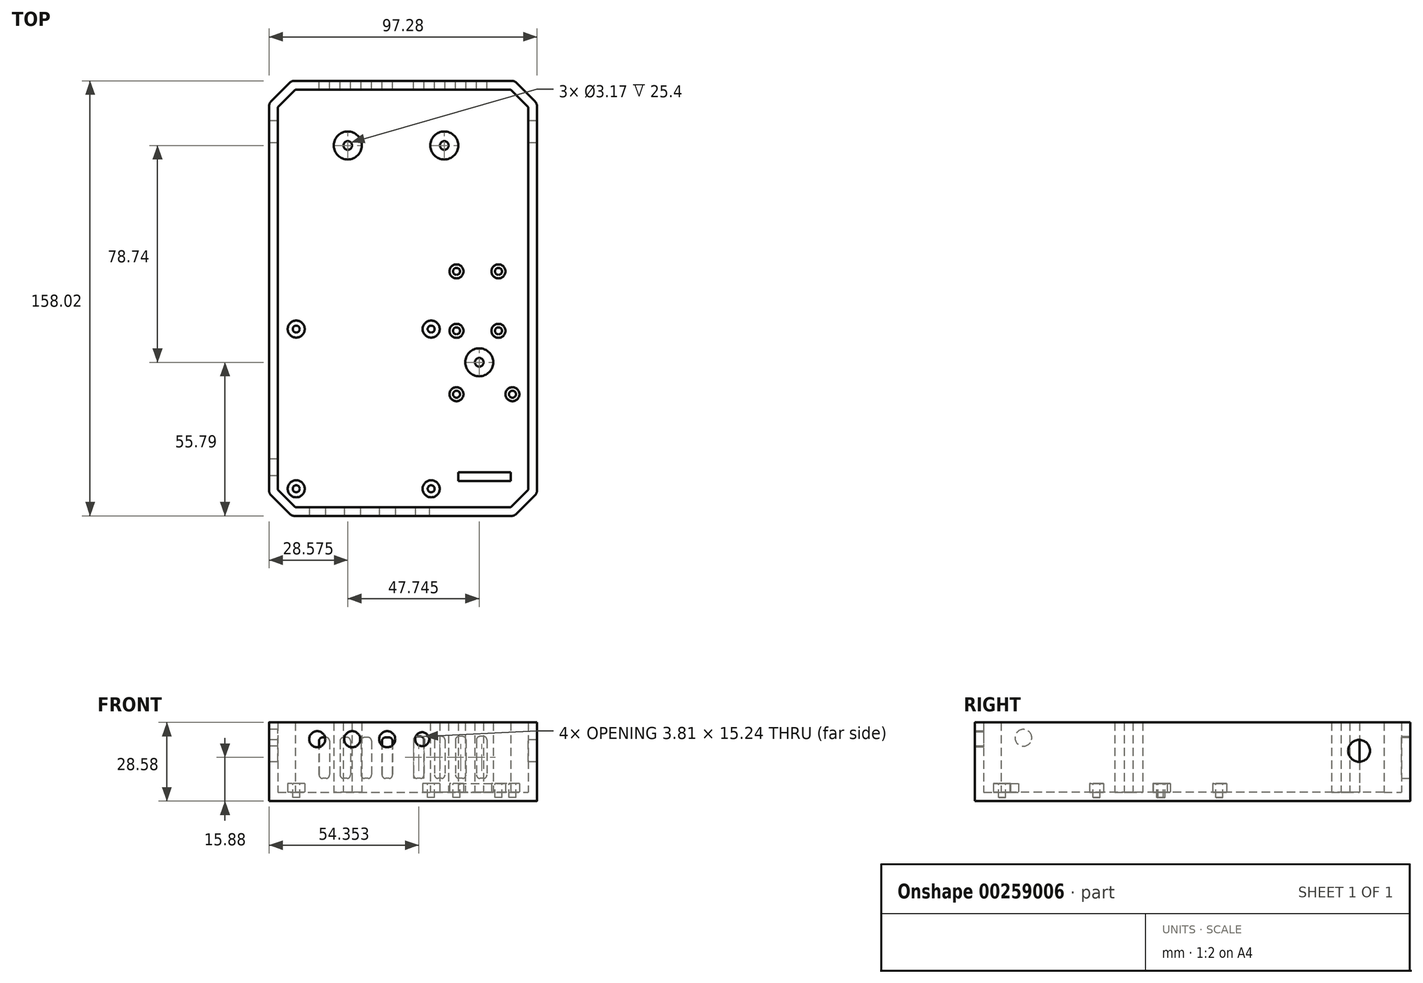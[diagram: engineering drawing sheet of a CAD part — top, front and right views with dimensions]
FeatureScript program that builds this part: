
annotation { "Feature Type Name" : "Feature", "Feature Type Description" : "" }
export const myFeature = defineFeature(function(context is Context, id is Id, definition is map)
    precondition{}
    {
        {
            var Q0;
            Q0=qCreatedBy(makeId("Top.planeOp"),FACE);
            var sketch = newSketch(context, id + "F0", { "sketchPlane" : qUnion([Q0])});
            skLineSegment(sketch, "E0.bottom", {"start": v(-25, 46.5) * mm, "end": v(25, 46.5) * mm});
            skLineSegment(sketch, "E0.top", {"start": v(-25, -38.5) * mm, "end": v(25, -38.5) * mm});
            skLineSegment(sketch, "E0.left", {"start": v(-28, 43.5) * mm, "end": v(-28, -35.5) * mm});
            skLineSegment(sketch, "E0.right", {"start": v(28, 43.5) * mm, "end": v(28, -35.5) * mm});
            skCircle(sketch, "E1", {"center": v(-24.5, -35) * mm, "radius": 3.1 * mm});
            skCircle(sketch, "E2", {"center": v(24.5, -35) * mm, "radius": 3.1 * mm});
            skCircle(sketch, "E3", {"center": v(24.5, 23) * mm, "radius": 3.1 * mm});
            skCircle(sketch, "E4", {"center": v(-24.5, 23) * mm, "radius": 3.1 * mm});
            skCircle(sketch, "E5", {"center": v(-24.5, 23) * mm, "radius": 1.38 * mm});
            skCircle(sketch, "E6", {"center": v(24.5, 23) * mm, "radius": 1.38 * mm});
            skCircle(sketch, "E7", {"center": v(24.5, -35) * mm, "radius": 1.38 * mm});
            skCircle(sketch, "E8", {"center": v(-24.5, -35) * mm, "radius": 1.38 * mm});
            skPoint(sketch, "E9.visualSharp", {"position": v(-28, 46.5) * mm});
            skArc(sketch, "E9.filletArc", {"start": v(-25, 46.5) * mm, "mid": v(-27.12, 45.62) * mm, "end": v(-28, 43.5) * mm});
            skPoint(sketch, "E10.visualSharp", {"position": v(28, 46.5) * mm});
            skArc(sketch, "E10.filletArc", {"start": v(28, 43.5) * mm, "mid": v(27.12, 45.62) * mm, "end": v(25, 46.5) * mm});
            skPoint(sketch, "E11.visualSharp", {"position": v(-28, -38.5) * mm});
            skArc(sketch, "E11.filletArc", {"start": v(-28, -35.5) * mm, "mid": v(-27.12, -37.62) * mm, "end": v(-25, -38.5) * mm});
            skPoint(sketch, "E12.visualSharp", {"position": v(28, -38.5) * mm});
            skArc(sketch, "E12.filletArc", {"start": v(25, -38.5) * mm, "mid": v(27.12, -37.62) * mm, "end": v(28, -35.5) * mm});
            skSolve(sketch);
        }
        {
            var Q0;
            Q0=qCreatedBy(makeId("Top.planeOp"),FACE);
            var sketch = newSketch(context, id + "F1", { "sketchPlane" : qUnion([Q0])});
            skLineSegment(sketch, "E13.bottom", {"start": v(31.17, 46.5) * mm, "end": v(51.5, 46.5) * mm});
            skLineSegment(sketch, "E13.top", {"start": v(31.18, 19.83) * mm, "end": v(51.5, 19.83) * mm});
            skLineSegment(sketch, "E13.left", {"start": v(31.17, 46.5) * mm, "end": v(31.18, 19.83) * mm});
            skLineSegment(sketch, "E13.right", {"start": v(51.5, 46.5) * mm, "end": v(51.5, 19.83) * mm});
            skCircle(sketch, "E14", {"center": v(33.72, 43.96) * mm, "radius": 1.14 * mm});
            skCircle(sketch, "E15", {"center": v(48.95, 43.96) * mm, "radius": 1.14 * mm});
            skCircle(sketch, "E16", {"center": v(48.95, 22.37) * mm, "radius": 1.14 * mm});
            skCircle(sketch, "E17", {"center": v(33.72, 22.37) * mm, "radius": 1.14 * mm});
            skSolve(sketch);
        }
        {
            var Q0;
            Q0=qCreatedBy(makeId("Top.planeOp"),FACE);
            var sketch = newSketch(context, id + "F2", { "sketchPlane" : qUnion([Q0])});
            skLineSegment(sketch, "E18.bottom", {"start": v(31.18, 1.89) * mm, "end": v(56.58, 1.89) * mm});
            skLineSegment(sketch, "E18.top", {"start": v(31.18, -32.15) * mm, "end": v(56.58, -32.15) * mm});
            skLineSegment(sketch, "E18.left", {"start": v(31.18, 1.89) * mm, "end": v(31.18, -32.15) * mm});
            skLineSegment(sketch, "E18.right", {"start": v(56.57, 1.89) * mm, "end": v(56.57, -32.15) * mm});
            skCircle(sketch, "E19", {"center": v(33.72, -0.65) * mm, "radius": 1.14 * mm});
            skCircle(sketch, "E20", {"center": v(54.04, -0.65) * mm, "radius": 1.14 * mm});
            skSolve(sketch);
        }
        {
            var Q0;
            Q0=qCreatedBy(makeId("Top.planeOp"),FACE);
            var sketch = newSketch(context, id + "F3", { "sketchPlane" : qUnion([Q0])});
            skLineSegment(sketch, "E21.bottom", {"start": v(-24.83, 110) * mm, "end": v(53.4, 110) * mm});
            skLineSegment(sketch, "E21.top", {"start": v(-24.82, -41.68) * mm, "end": v(53.4, -41.68) * mm});
            skLineSegment(sketch, "E21.left", {"start": v(-31.18, 103.65) * mm, "end": v(-31.17, -35.33) * mm});
            skLineSegment(sketch, "E21.right", {"start": v(59.75, 103.65) * mm, "end": v(59.75, -35.33) * mm});
            skLineSegment(sketch, "E22", {"start": v(-31.18, 103.65) * mm, "end": v(-24.83, 110) * mm});
            skLineSegment(sketch, "E23", {"start": v(53.4, 110) * mm, "end": v(59.75, 103.65) * mm});
            skLineSegment(sketch, "E24", {"start": v(-31.17, -35.33) * mm, "end": v(-24.82, -41.68) * mm});
            skLineSegment(sketch, "E25", {"start": v(53.4, -41.67) * mm, "end": v(59.75, -35.33) * mm});
            skPoint(sketch, "E26.orphan", {"position": v(-31.18, 110) * mm});
            skPoint(sketch, "E27.orphan", {"position": v(59.75, 110) * mm});
            skPoint(sketch, "E28.orphan", {"position": v(59.75, -41.68) * mm});
            skPoint(sketch, "E29.orphan", {"position": v(-31.17, -41.68) * mm});
            skLineSegment(sketch, "E30.0", {"start": v(-34.35, 104.97) * mm, "end": v(-26.14, 113.18) * mm});
            skLineSegment(sketch, "E30.1", {"start": v(-26.14, 113.18) * mm, "end": v(54.72, 113.18) * mm});
            skLineSegment(sketch, "E30.2", {"start": v(-34.35, 104.97) * mm, "end": v(-34.35, -36.64) * mm});
            skLineSegment(sketch, "E30.3", {"start": v(54.72, 113.18) * mm, "end": v(62.92, 104.97) * mm});
            skLineSegment(sketch, "E30.4", {"start": v(-34.35, -36.64) * mm, "end": v(-26.14, -44.85) * mm});
            skLineSegment(sketch, "E30.5", {"start": v(-26.14, -44.85) * mm, "end": v(54.72, -44.85) * mm});
            skLineSegment(sketch, "E30.6", {"start": v(54.72, -44.85) * mm, "end": v(62.92, -36.64) * mm});
            skLineSegment(sketch, "E30.7", {"start": v(62.92, 104.97) * mm, "end": v(62.92, -36.64) * mm});
            skSolve(sketch);
        }
        {
            var Q0;
            Q0=makeQuery(id+"F3.imprint","IMPRINT",FACE,{"disambiguationData":[TD([[makeQuery(id+"F3.imprint","IMPRINT",EDGE,{"derivedFrom":sQuery(id+"F3.wireOp",EDGE,"E21.bottom")}),-1.0]])]});
            var Q1;
            Q1=makeQuery(id+"F3.imprint","IMPRINT",FACE,{"disambiguationData":[TD([[makeQuery(id+"F3.imprint","IMPRINT",EDGE,{"derivedFrom":sQuery(id+"F3.wireOp",EDGE,"E21.bottom")}),1.0]])]});
            extrude(context, id + "F4", {"entities" : qUnion([Q0, Q1]), "oppositeDirection" : true, "depth" : 3.17 * mm});
        }
        {
            var Q0;
            Q0=makeQuery(id+"F3.imprint","IMPRINT",FACE,{"disambiguationData":[TD([[makeQuery(id+"F3.imprint","IMPRINT",EDGE,{"derivedFrom":sQuery(id+"F3.wireOp",EDGE,"E21.bottom")}),1.0]])]});
            extrude(context, id + "F5", {"entities" : qUnion([Q0]), "operationType" : NewBodyOperationType.ADD, "depth" : 25.4 * mm});
        }
        {
            var Q0;
            Q0=makeQuery(id+"F3.imprint","IMPRINT",FACE,{"disambiguationData":[TD([[makeQuery(id+"F3.imprint","IMPRINT",EDGE,{"derivedFrom":sQuery(id+"F3.wireOp",EDGE,"E21.bottom")}),-1.0]])]});
            var sketch = newSketch(context, id + "F6", { "sketchPlane" : qUnion([Q0])});
            skCircle(sketch, "E31", {"center": v(-24.5, 23) * mm, "radius": 3.1 * mm});
            skCircle(sketch, "E32", {"center": v(24.5, 23) * mm, "radius": 3.1 * mm});
            skCircle(sketch, "E33", {"center": v(-24.5, -35) * mm, "radius": 3.1 * mm});
            skCircle(sketch, "E34", {"center": v(24.5, -35) * mm, "radius": 3.1 * mm});
            skCircle(sketch, "E35", {"center": v(33.72, 43.96) * mm, "radius": 2.54 * mm});
            skCircle(sketch, "E36", {"center": v(48.95, 43.96) * mm, "radius": 2.54 * mm});
            skCircle(sketch, "E37", {"center": v(33.72, 22.37) * mm, "radius": 2.54 * mm});
            skCircle(sketch, "E38", {"center": v(48.95, 22.37) * mm, "radius": 2.54 * mm});
            skCircle(sketch, "E39", {"center": v(33.72, -0.65) * mm, "radius": 2.54 * mm});
            skCircle(sketch, "E40", {"center": v(54.04, -0.65) * mm, "radius": 2.54 * mm});
            skLineSegment(sketch, "E41.bottom", {"start": v(34.35, -32.15) * mm, "end": v(53.4, -32.15) * mm});
            skLineSegment(sketch, "E41.top", {"start": v(34.35, -28.97) * mm, "end": v(53.4, -28.97) * mm});
            skLineSegment(sketch, "E41.left", {"start": v(34.35, -32.15) * mm, "end": v(34.35, -28.97) * mm});
            skLineSegment(sketch, "E41.right", {"start": v(53.4, -32.15) * mm, "end": v(53.4, -28.97) * mm});
            skSolve(sketch);
        }
        {
            var Q0;
            Q0 = qSketchRegion(id + "F6", true);
            var Q1;
            Q1=makeQuery(id+"F0.imprint","IMPRINT",FACE,{"disambiguationData":[TD([[makeQuery(id+"F0.imprint","IMPRINT",EDGE,{"derivedFrom":sQuery(id+"F0.wireOp",EDGE,"E4")}),1.0]])]});
            extrude(context, id + "F7", {"entities" : qUnion([Q0, Q1]), "operationType" : NewBodyOperationType.ADD, "depth" : 3.17 * mm});
        }
        {
            var Q0;
            Q0=makeQuery(id+"F7.boolean.opBoolean","MERGE",FACE,{"derivedFrom":[makeQuery(id+"F7.opExtrude","CAP_FACE",FACE,{"disambiguationData":[OSD([sQuery(id+"F0.wireOp",EDGE,"E4"),sQuery(id+"F0.wireOp",EDGE,"E5")])],"isStart":false}),makeQuery(id+"F7.opExtrude","CAP_FACE",FACE,{"disambiguationData":[OSD([sQuery(id+"F6.wireOp",EDGE,"E31")])],"isStart":false})]});
            var sketch = newSketch(context, id + "F8", { "sketchPlane" : qUnion([Q0])});
            skCircle(sketch, "E42", {"center": v(-24.5, 23) * mm, "radius": 1.27 * mm});
            skCircle(sketch, "E43", {"center": v(24.5, 23) * mm, "radius": 1.27 * mm});
            skCircle(sketch, "E44", {"center": v(24.5, -35) * mm, "radius": 1.27 * mm});
            skCircle(sketch, "E45", {"center": v(-24.5, -35) * mm, "radius": 1.27 * mm});
            skCircle(sketch, "E46", {"center": v(33.72, 43.96) * mm, "radius": 1.27 * mm});
            skCircle(sketch, "E47", {"center": v(48.95, 43.96) * mm, "radius": 1.27 * mm});
            skCircle(sketch, "E48", {"center": v(33.72, 22.37) * mm, "radius": 1.27 * mm});
            skCircle(sketch, "E49", {"center": v(48.95, 22.37) * mm, "radius": 1.27 * mm});
            skCircle(sketch, "E50", {"center": v(33.72, -0.65) * mm, "radius": 1.27 * mm});
            skCircle(sketch, "E51", {"center": v(54.04, -0.65) * mm, "radius": 1.27 * mm});
            skSolve(sketch);
        }
        {
            var Q0;
            Q0 = qSketchRegion(id + "F8", true);
            extrude(context, id + "F9", {"entities" : qUnion([Q0]), "operationType" : NewBodyOperationType.REMOVE, "oppositeDirection" : true, "depth" : 5.08 * mm});
        }
        {
            var Q0;
            {var subQ0=sQuery(id+"F3.wireOp",EDGE,"E30.2");Q0=makeQuery(id+"F5.boolean.opBoolean","MERGE",FACE,{"derivedFrom":[makeQuery(id+"F4.opExtrude","SWEPT_FACE",FACE,{"disambiguationData":[OSD([subQ0])]}),makeQuery(id+"F5.opExtrude","SWEPT_FACE",FACE,{"disambiguationData":[OSD([subQ0])]})]});}
            var sketch = newSketch(context, id + "F10", { "sketchPlane" : qUnion([Q0])});
            skCircle(sketch, "E52", {"center": v(27.24, 19.81) * mm, "radius": 3.05 * mm});
            skSolve(sketch);
        }
        {
            var Q0;
            Q0 = qSketchRegion(id + "F10", true);
            extrude(context, id + "F11", {"entities" : qUnion([Q0]), "operationType" : NewBodyOperationType.REMOVE, "endBound" : BoundingType.UP_TO_NEXT, "oppositeDirection" : true, "depth" : 25.4 * mm});
        }
        {
            var Q0;
            {var subQ0=sQuery(id+"F3.wireOp",EDGE,"E30.2");Q0=makeQuery(id+"F5.boolean.opBoolean","MERGE",FACE,{"derivedFrom":[makeQuery(id+"F4.opExtrude","SWEPT_FACE",FACE,{"disambiguationData":[OSD([subQ0])]}),makeQuery(id+"F5.opExtrude","SWEPT_FACE",FACE,{"disambiguationData":[OSD([subQ0])]})]});}
            var sketch = newSketch(context, id + "F12", { "sketchPlane" : qUnion([Q0])});
            skCircle(sketch, "E53", {"center": v(-94.65, 15.08) * mm, "radius": 3.97 * mm});
            skSolve(sketch);
        }
        {
            var Q0;
            Q0=makeQuery(id+"F12.imprint","IMPRINT",FACE,{"disambiguationData":[TD([[makeQuery(id+"F12.imprint","IMPRINT",EDGE,{"derivedFrom":sQuery(id+"F12.wireOp",EDGE,"E53")}),1.0]])]});
            extrude(context, id + "F13", {"entities" : qUnion([Q0]), "operationType" : NewBodyOperationType.REMOVE, "endBound" : BoundingType.THROUGH_ALL, "oppositeDirection" : true, "depth" : 25.4 * mm});
        }
        {
            var Q0;
            {var subQ0=sQuery(id+"F3.wireOp",EDGE,"E30.1");Q0=makeQuery(id+"F5.boolean.opBoolean","MERGE",FACE,{"derivedFrom":[makeQuery(id+"F4.opExtrude","SWEPT_FACE",FACE,{"disambiguationData":[OSD([subQ0])]}),makeQuery(id+"F5.opExtrude","SWEPT_FACE",FACE,{"disambiguationData":[OSD([subQ0])]})]});}
            var sketch = newSketch(context, id + "F14", { "sketchPlane" : qUnion([Q0])});
            skLineSegment(sketch, "E54", {"start": v(-14.29, 25.4) * mm, "end": v(-14.29, 0) * mm});
            skLineSegment(sketch, "E55.bottom", {"start": v(-20.64, 20.32) * mm, "end": v(-19.37, 20.32) * mm});
            skLineSegment(sketch, "E55.top", {"start": v(-20.64, 5.08) * mm, "end": v(-19.37, 5.08) * mm});
            skLineSegment(sketch, "E55.left", {"start": v(-21.9, 19.05) * mm, "end": v(-21.9, 6.35) * mm});
            skLineSegment(sketch, "E55.right", {"start": v(-18.1, 19.05) * mm, "end": v(-18.1, 6.35) * mm});
            skPoint(sketch, "E56.visualSharp", {"position": v(-21.9, 20.32) * mm});
            skArc(sketch, "E56.filletArc", {"start": v(-20.64, 20.32) * mm, "mid": v(-21.54, 19.95) * mm, "end": v(-21.9, 19.05) * mm});
            skPoint(sketch, "E57.visualSharp", {"position": v(-18.1, 20.32) * mm});
            skArc(sketch, "E57.filletArc", {"start": v(-18.1, 19.05) * mm, "mid": v(-18.47, 19.95) * mm, "end": v(-19.37, 20.32) * mm});
            skPoint(sketch, "E58.visualSharp", {"position": v(-21.9, 5.08) * mm});
            skArc(sketch, "E58.filletArc", {"start": v(-21.9, 6.35) * mm, "mid": v(-21.54, 5.45) * mm, "end": v(-20.64, 5.08) * mm});
            skPoint(sketch, "E59.visualSharp", {"position": v(-18.1, 5.08) * mm});
            skArc(sketch, "E59.filletArc", {"start": v(-19.37, 5.08) * mm, "mid": v(-18.47, 5.45) * mm, "end": v(-18.1, 6.35) * mm});
            skPoint(sketch, "E60.1.0.0", {"position": v(-29.53, 5.08) * mm});
            skLineSegment(sketch, "E60.1.0.1", {"start": v(-25.72, 19.05) * mm, "end": v(-25.72, 6.35) * mm});
            skPoint(sketch, "E60.1.0.2", {"position": v(-25.72, 5.08) * mm});
            skLineSegment(sketch, "E60.1.0.3", {"start": v(-29.53, 19.05) * mm, "end": v(-29.53, 6.35) * mm});
            skPoint(sketch, "E60.1.0.4", {"position": v(-25.72, 20.32) * mm});
            skPoint(sketch, "E60.1.0.5", {"position": v(-29.53, 20.32) * mm});
            skArc(sketch, "E60.1.0.6", {"start": v(-25.72, 19.05) * mm, "mid": v(-26.09, 19.95) * mm, "end": v(-26.99, 20.32) * mm});
            skArc(sketch, "E60.1.0.7", {"start": v(-28.26, 20.32) * mm, "mid": v(-29.16, 19.95) * mm, "end": v(-29.53, 19.05) * mm});
            skArc(sketch, "E60.1.0.8", {"start": v(-29.53, 6.35) * mm, "mid": v(-29.16, 5.45) * mm, "end": v(-28.26, 5.08) * mm});
            skArc(sketch, "E60.1.0.9", {"start": v(-26.99, 5.08) * mm, "mid": v(-26.09, 5.45) * mm, "end": v(-25.72, 6.35) * mm});
            skLineSegment(sketch, "E60.1.0.10", {"start": v(-28.26, 20.32) * mm, "end": v(-26.99, 20.32) * mm});
            skLineSegment(sketch, "E60.1.0.11", {"start": v(-28.26, 5.08) * mm, "end": v(-26.99, 5.08) * mm});
            skPoint(sketch, "E60.2.0.0", {"position": v(-37.15, 5.08) * mm});
            skLineSegment(sketch, "E60.2.0.1", {"start": v(-33.34, 19.05) * mm, "end": v(-33.34, 6.35) * mm});
            skPoint(sketch, "E60.2.0.2", {"position": v(-33.34, 5.08) * mm});
            skLineSegment(sketch, "E60.2.0.3", {"start": v(-37.15, 19.05) * mm, "end": v(-37.15, 6.35) * mm});
            skPoint(sketch, "E60.2.0.4", {"position": v(-33.34, 20.32) * mm});
            skPoint(sketch, "E60.2.0.5", {"position": v(-37.15, 20.32) * mm});
            skArc(sketch, "E60.2.0.6", {"start": v(-33.34, 19.05) * mm, "mid": v(-33.7, 19.95) * mm, "end": v(-34.6, 20.32) * mm});
            skArc(sketch, "E60.2.0.7", {"start": v(-35.88, 20.32) * mm, "mid": v(-36.78, 19.95) * mm, "end": v(-37.15, 19.05) * mm});
            skArc(sketch, "E60.2.0.8", {"start": v(-37.15, 6.35) * mm, "mid": v(-36.78, 5.45) * mm, "end": v(-35.88, 5.08) * mm});
            skArc(sketch, "E60.2.0.9", {"start": v(-34.6, 5.08) * mm, "mid": v(-33.7, 5.45) * mm, "end": v(-33.34, 6.35) * mm});
            skLineSegment(sketch, "E60.2.0.10", {"start": v(-35.88, 20.32) * mm, "end": v(-34.6, 20.32) * mm});
            skLineSegment(sketch, "E60.2.0.11", {"start": v(-35.88, 5.08) * mm, "end": v(-34.6, 5.08) * mm});
            skPoint(sketch, "E60.3.0.0", {"position": v(-44.77, 5.08) * mm});
            skLineSegment(sketch, "E60.3.0.1", {"start": v(-40.96, 19.05) * mm, "end": v(-40.96, 6.35) * mm});
            skPoint(sketch, "E60.3.0.2", {"position": v(-40.96, 5.08) * mm});
            skLineSegment(sketch, "E60.3.0.3", {"start": v(-44.77, 19.05) * mm, "end": v(-44.77, 6.35) * mm});
            skPoint(sketch, "E60.3.0.4", {"position": v(-40.96, 20.32) * mm});
            skPoint(sketch, "E60.3.0.5", {"position": v(-44.77, 20.32) * mm});
            skArc(sketch, "E60.3.0.6", {"start": v(-40.96, 19.05) * mm, "mid": v(-41.33, 19.95) * mm, "end": v(-42.23, 20.32) * mm});
            skArc(sketch, "E60.3.0.7", {"start": v(-43.5, 20.32) * mm, "mid": v(-44.4, 19.95) * mm, "end": v(-44.77, 19.05) * mm});
            skArc(sketch, "E60.3.0.8", {"start": v(-44.77, 6.35) * mm, "mid": v(-44.4, 5.45) * mm, "end": v(-43.5, 5.08) * mm});
            skArc(sketch, "E60.3.0.9", {"start": v(-42.23, 5.08) * mm, "mid": v(-41.33, 5.45) * mm, "end": v(-40.96, 6.35) * mm});
            skLineSegment(sketch, "E60.3.0.10", {"start": v(-43.5, 20.32) * mm, "end": v(-42.23, 20.32) * mm});
            skLineSegment(sketch, "E60.3.0.11", {"start": v(-43.5, 5.08) * mm, "end": v(-42.23, 5.08) * mm});
            skLineSegment(sketch, "E60.direction1", {"start": v(-21.9, 5.08) * mm, "end": v(-29.53, 5.08) * mm, "construction": true});
            skPoint(sketch, "E61.firstSnap0", {"position": v(-18.47, 19.95) * mm});
            skLineSegment(sketch, "E61.bottom", {"start": v(-9.2, 19.95) * mm, "end": v(-7.94, 19.95) * mm});
            skLineSegment(sketch, "E61.top", {"start": v(-9.2, 5.08) * mm, "end": v(-7.94, 5.08) * mm});
            skLineSegment(sketch, "E61.left", {"start": v(-10.48, 18.68) * mm, "end": v(-10.48, 6.35) * mm});
            skLineSegment(sketch, "E61.right", {"start": v(-6.67, 18.68) * mm, "end": v(-6.67, 6.35) * mm});
            skPoint(sketch, "E62.visualSharp", {"position": v(-10.48, 19.95) * mm});
            skArc(sketch, "E62.filletArc", {"start": v(-9.2, 19.95) * mm, "mid": v(-10.1, 19.58) * mm, "end": v(-10.48, 18.68) * mm});
            skPoint(sketch, "E63.visualSharp", {"position": v(-6.67, 19.95) * mm});
            skArc(sketch, "E63.filletArc", {"start": v(-6.67, 18.68) * mm, "mid": v(-7.04, 19.58) * mm, "end": v(-7.94, 19.95) * mm});
            skPoint(sketch, "E64.visualSharp", {"position": v(-10.48, 5.08) * mm});
            skArc(sketch, "E64.filletArc", {"start": v(-10.48, 6.35) * mm, "mid": v(-10.1, 5.45) * mm, "end": v(-9.2, 5.08) * mm});
            skPoint(sketch, "E65.visualSharp", {"position": v(-6.67, 5.08) * mm});
            skArc(sketch, "E65.filletArc", {"start": v(-7.94, 5.08) * mm, "mid": v(-7.04, 5.45) * mm, "end": v(-6.67, 6.35) * mm});
            skPoint(sketch, "E66.1.0.0", {"position": v(0.95, 5.08) * mm});
            skPoint(sketch, "E66.1.0.1", {"position": v(0.95, 19.95) * mm});
            skPoint(sketch, "E66.1.0.2", {"position": v(-2.86, 5.08) * mm});
            skPoint(sketch, "E66.1.0.3", {"position": v(-2.86, 19.95) * mm});
            skLineSegment(sketch, "E66.1.0.4", {"start": v(-2.86, 18.68) * mm, "end": v(-2.86, 6.35) * mm});
            skLineSegment(sketch, "E66.1.0.5", {"start": v(0.95, 18.68) * mm, "end": v(0.95, 6.35) * mm});
            skArc(sketch, "E66.1.0.6", {"start": v(-0.32, 5.08) * mm, "mid": v(0.58, 5.45) * mm, "end": v(0.95, 6.35) * mm});
            skArc(sketch, "E66.1.0.7", {"start": v(-2.86, 6.35) * mm, "mid": v(-2.49, 5.45) * mm, "end": v(-1.59, 5.08) * mm});
            skArc(sketch, "E66.1.0.8", {"start": v(-1.59, 19.95) * mm, "mid": v(-2.49, 19.58) * mm, "end": v(-2.86, 18.68) * mm});
            skArc(sketch, "E66.1.0.9", {"start": v(0.95, 18.68) * mm, "mid": v(0.58, 19.58) * mm, "end": v(-0.32, 19.95) * mm});
            skLineSegment(sketch, "E66.1.0.10", {"start": v(-1.59, 5.08) * mm, "end": v(-0.32, 5.08) * mm});
            skLineSegment(sketch, "E66.1.0.11", {"start": v(-1.59, 19.95) * mm, "end": v(-0.32, 19.95) * mm});
            skPoint(sketch, "E66.2.0.0", {"position": v(8.57, 5.08) * mm});
            skPoint(sketch, "E66.2.0.1", {"position": v(8.57, 19.95) * mm});
            skPoint(sketch, "E66.2.0.2", {"position": v(4.76, 5.08) * mm});
            skPoint(sketch, "E66.2.0.3", {"position": v(4.76, 19.95) * mm});
            skLineSegment(sketch, "E66.2.0.4", {"start": v(4.76, 18.68) * mm, "end": v(4.76, 6.35) * mm});
            skLineSegment(sketch, "E66.2.0.5", {"start": v(8.57, 18.68) * mm, "end": v(8.57, 6.35) * mm});
            skArc(sketch, "E66.2.0.6", {"start": v(7.3, 5.08) * mm, "mid": v(8.2, 5.45) * mm, "end": v(8.57, 6.35) * mm});
            skArc(sketch, "E66.2.0.7", {"start": v(4.76, 6.35) * mm, "mid": v(5.13, 5.45) * mm, "end": v(6.03, 5.08) * mm});
            skArc(sketch, "E66.2.0.8", {"start": v(6.03, 19.95) * mm, "mid": v(5.13, 19.58) * mm, "end": v(4.76, 18.68) * mm});
            skArc(sketch, "E66.2.0.9", {"start": v(8.57, 18.68) * mm, "mid": v(8.2, 19.58) * mm, "end": v(7.3, 19.95) * mm});
            skLineSegment(sketch, "E66.2.0.10", {"start": v(6.03, 5.08) * mm, "end": v(7.3, 5.08) * mm});
            skLineSegment(sketch, "E66.2.0.11", {"start": v(6.03, 19.95) * mm, "end": v(7.3, 19.95) * mm});
            skPoint(sketch, "E66.3.0.0", {"position": v(16.2, 5.08) * mm});
            skPoint(sketch, "E66.3.0.1", {"position": v(16.2, 19.95) * mm});
            skPoint(sketch, "E66.3.0.2", {"position": v(12.38, 5.08) * mm});
            skPoint(sketch, "E66.3.0.3", {"position": v(12.38, 19.95) * mm});
            skLineSegment(sketch, "E66.3.0.4", {"start": v(12.38, 18.68) * mm, "end": v(12.38, 6.35) * mm});
            skLineSegment(sketch, "E66.3.0.5", {"start": v(16.2, 18.68) * mm, "end": v(16.2, 6.35) * mm});
            skArc(sketch, "E66.3.0.6", {"start": v(14.92, 5.08) * mm, "mid": v(15.82, 5.45) * mm, "end": v(16.2, 6.35) * mm});
            skArc(sketch, "E66.3.0.7", {"start": v(12.38, 6.35) * mm, "mid": v(12.75, 5.45) * mm, "end": v(13.65, 5.08) * mm});
            skArc(sketch, "E66.3.0.8", {"start": v(13.65, 19.95) * mm, "mid": v(12.75, 19.58) * mm, "end": v(12.38, 18.68) * mm});
            skArc(sketch, "E66.3.0.9", {"start": v(16.2, 18.68) * mm, "mid": v(15.82, 19.58) * mm, "end": v(14.92, 19.95) * mm});
            skLineSegment(sketch, "E66.3.0.10", {"start": v(13.65, 5.08) * mm, "end": v(14.92, 5.08) * mm});
            skLineSegment(sketch, "E66.3.0.11", {"start": v(13.65, 19.95) * mm, "end": v(14.92, 19.95) * mm});
            skLineSegment(sketch, "E66.direction1", {"start": v(-10.48, 5.08) * mm, "end": v(-2.86, 5.08) * mm, "construction": true});
            skSolve(sketch);
        }
        {
            var Q0;
            Q0 = qSketchRegion(id + "F14", true);
            extrude(context, id + "F15", {"entities" : qUnion([Q0]), "operationType" : NewBodyOperationType.REMOVE, "endBound" : BoundingType.UP_TO_NEXT, "oppositeDirection" : true, "depth" : 25.4 * mm});
        }
        {
            var Q0;
            {var subQ0=sQuery(id+"F3.wireOp",EDGE,"E30.5");Q0=makeQuery(id+"F5.boolean.opBoolean","MERGE",FACE,{"derivedFrom":[makeQuery(id+"F4.opExtrude","SWEPT_FACE",FACE,{"disambiguationData":[OSD([subQ0])]}),makeQuery(id+"F5.opExtrude","SWEPT_FACE",FACE,{"disambiguationData":[OSD([subQ0])]})]});}
            var sketch = newSketch(context, id + "F16", { "sketchPlane" : qUnion([Q0])});
            skCircle(sketch, "E67", {"center": v(-16.87, 19.3) * mm, "radius": 2.92 * mm});
            skCircle(sketch, "E68", {"center": v(-4.17, 19.3) * mm, "radius": 2.92 * mm});
            skCircle(sketch, "E69", {"center": v(8.53, 19.3) * mm, "radius": 2.92 * mm});
            skCircle(sketch, "E70", {"center": v(21.23, 19.3) * mm, "radius": 2.54 * mm});
            skSolve(sketch);
        }
        {
            var Q0;
            Q0 = qSketchRegion(id + "F16", true);
            extrude(context, id + "F17", {"entities" : qUnion([Q0]), "operationType" : NewBodyOperationType.REMOVE, "endBound" : BoundingType.UP_TO_NEXT, "oppositeDirection" : true, "depth" : 25.4 * mm});
        }
        {
            var Q0;
            {var subQ0=sQuery(id+"F3.wireOp",EDGE,"E30.7");var subQ1=sQuery(id+"F3.wireOp",EDGE,"E30.6");Q0=makeQuery(id+"F5.boolean.opBoolean","MERGE",EDGE,{"derivedFrom":[makeQuery(id+"F4.opExtrude","SWEPT_EDGE",EDGE,{"disambiguationData":[OSD([subQ1,subQ0])]}),makeQuery(id+"F5.opExtrude","SWEPT_EDGE",EDGE,{"disambiguationData":[OSD([subQ1,subQ0])]})]});}
            var Q1;
            {var subQ0=sQuery(id+"F3.wireOp",EDGE,"E30.6");var subQ1=sQuery(id+"F3.wireOp",EDGE,"E30.5");Q1=makeQuery(id+"F5.boolean.opBoolean","MERGE",EDGE,{"derivedFrom":[makeQuery(id+"F4.opExtrude","SWEPT_EDGE",EDGE,{"disambiguationData":[OSD([subQ1,subQ0])]}),makeQuery(id+"F5.opExtrude","SWEPT_EDGE",EDGE,{"disambiguationData":[OSD([subQ1,subQ0])]})]});}
            var Q2;
            {var subQ0=sQuery(id+"F3.wireOp",EDGE,"E30.7");var subQ1=sQuery(id+"F3.wireOp",EDGE,"E30.3");Q2=makeQuery(id+"F5.boolean.opBoolean","MERGE",EDGE,{"derivedFrom":[makeQuery(id+"F4.opExtrude","SWEPT_EDGE",EDGE,{"disambiguationData":[OSD([subQ1,subQ0])]}),makeQuery(id+"F5.opExtrude","SWEPT_EDGE",EDGE,{"disambiguationData":[OSD([subQ1,subQ0])]})]});}
            var Q3;
            {var subQ0=sQuery(id+"F3.wireOp",EDGE,"E30.3");var subQ1=sQuery(id+"F3.wireOp",EDGE,"E30.1");Q3=makeQuery(id+"F5.boolean.opBoolean","MERGE",EDGE,{"derivedFrom":[makeQuery(id+"F4.opExtrude","SWEPT_EDGE",EDGE,{"disambiguationData":[OSD([subQ1,subQ0])]}),makeQuery(id+"F5.opExtrude","SWEPT_EDGE",EDGE,{"disambiguationData":[OSD([subQ1,subQ0])]})]});}
            var Q4;
            {var subQ0=sQuery(id+"F3.wireOp",EDGE,"E30.1");var subQ1=sQuery(id+"F3.wireOp",EDGE,"E30.0");Q4=makeQuery(id+"F5.boolean.opBoolean","MERGE",EDGE,{"derivedFrom":[makeQuery(id+"F4.opExtrude","SWEPT_EDGE",EDGE,{"disambiguationData":[OSD([subQ1,subQ0])]}),makeQuery(id+"F5.opExtrude","SWEPT_EDGE",EDGE,{"disambiguationData":[OSD([subQ1,subQ0])]})]});}
            var Q5;
            {var subQ0=sQuery(id+"F3.wireOp",EDGE,"E30.2");var subQ1=sQuery(id+"F3.wireOp",EDGE,"E30.0");Q5=makeQuery(id+"F5.boolean.opBoolean","MERGE",EDGE,{"derivedFrom":[makeQuery(id+"F4.opExtrude","SWEPT_EDGE",EDGE,{"disambiguationData":[OSD([subQ1,subQ0])]}),makeQuery(id+"F5.opExtrude","SWEPT_EDGE",EDGE,{"disambiguationData":[OSD([subQ1,subQ0])]})]});}
            var Q6;
            {var subQ0=sQuery(id+"F3.wireOp",EDGE,"E30.4");var subQ1=sQuery(id+"F3.wireOp",EDGE,"E30.2");Q6=makeQuery(id+"F5.boolean.opBoolean","MERGE",EDGE,{"derivedFrom":[makeQuery(id+"F4.opExtrude","SWEPT_EDGE",EDGE,{"disambiguationData":[OSD([subQ1,subQ0])]}),makeQuery(id+"F5.opExtrude","SWEPT_EDGE",EDGE,{"disambiguationData":[OSD([subQ1,subQ0])]})]});}
            var Q7;
            {var subQ0=sQuery(id+"F3.wireOp",EDGE,"E30.5");var subQ1=sQuery(id+"F3.wireOp",EDGE,"E30.4");Q7=makeQuery(id+"F5.boolean.opBoolean","MERGE",EDGE,{"derivedFrom":[makeQuery(id+"F4.opExtrude","SWEPT_EDGE",EDGE,{"disambiguationData":[OSD([subQ1,subQ0])]}),makeQuery(id+"F5.opExtrude","SWEPT_EDGE",EDGE,{"disambiguationData":[OSD([subQ1,subQ0])]})]});}
            fillet(context, id + "F18", {"entities" : qUnion([Q0, Q1, Q2, Q3, Q4, Q5, Q6, Q7]), "radius" : 2.54 * mm, "tangentPropagation" : true, "allowEdgeOverflow" : false});
        }
        {
            var Q0;
            Q0=makeQuery(id+"F3.imprint","IMPRINT",FACE,{"disambiguationData":[TD([[makeQuery(id+"F3.imprint","IMPRINT",EDGE,{"derivedFrom":sQuery(id+"F3.wireOp",EDGE,"E21.bottom")}),-1.0]])]});
            var sketch = newSketch(context, id + "F19", { "sketchPlane" : qUnion([Q0])});
            skCircle(sketch, "E71", {"center": v(-5.78, 89.68) * mm, "radius": 5.08 * mm});
            skCircle(sketch, "E72", {"center": v(29.27, 89.68) * mm, "radius": 5.08 * mm});
            skCircle(sketch, "E73", {"center": v(41.97, 10.94) * mm, "radius": 5.08 * mm});
            skCircle(sketch, "E74", {"center": v(-5.78, 89.68) * mm, "radius": 1.59 * mm});
            skCircle(sketch, "E75", {"center": v(29.27, 89.68) * mm, "radius": 1.59 * mm});
            skCircle(sketch, "E76", {"center": v(41.97, 10.94) * mm, "radius": 1.59 * mm});
            skSolve(sketch);
        }
        {
            var Q0;
            Q0 = qSketchRegion(id + "F19", true);
            extrude(context, id + "F20", {"entities" : qUnion([Q0]), "operationType" : NewBodyOperationType.ADD, "depth" : 25.4 * mm});
        }
    });
